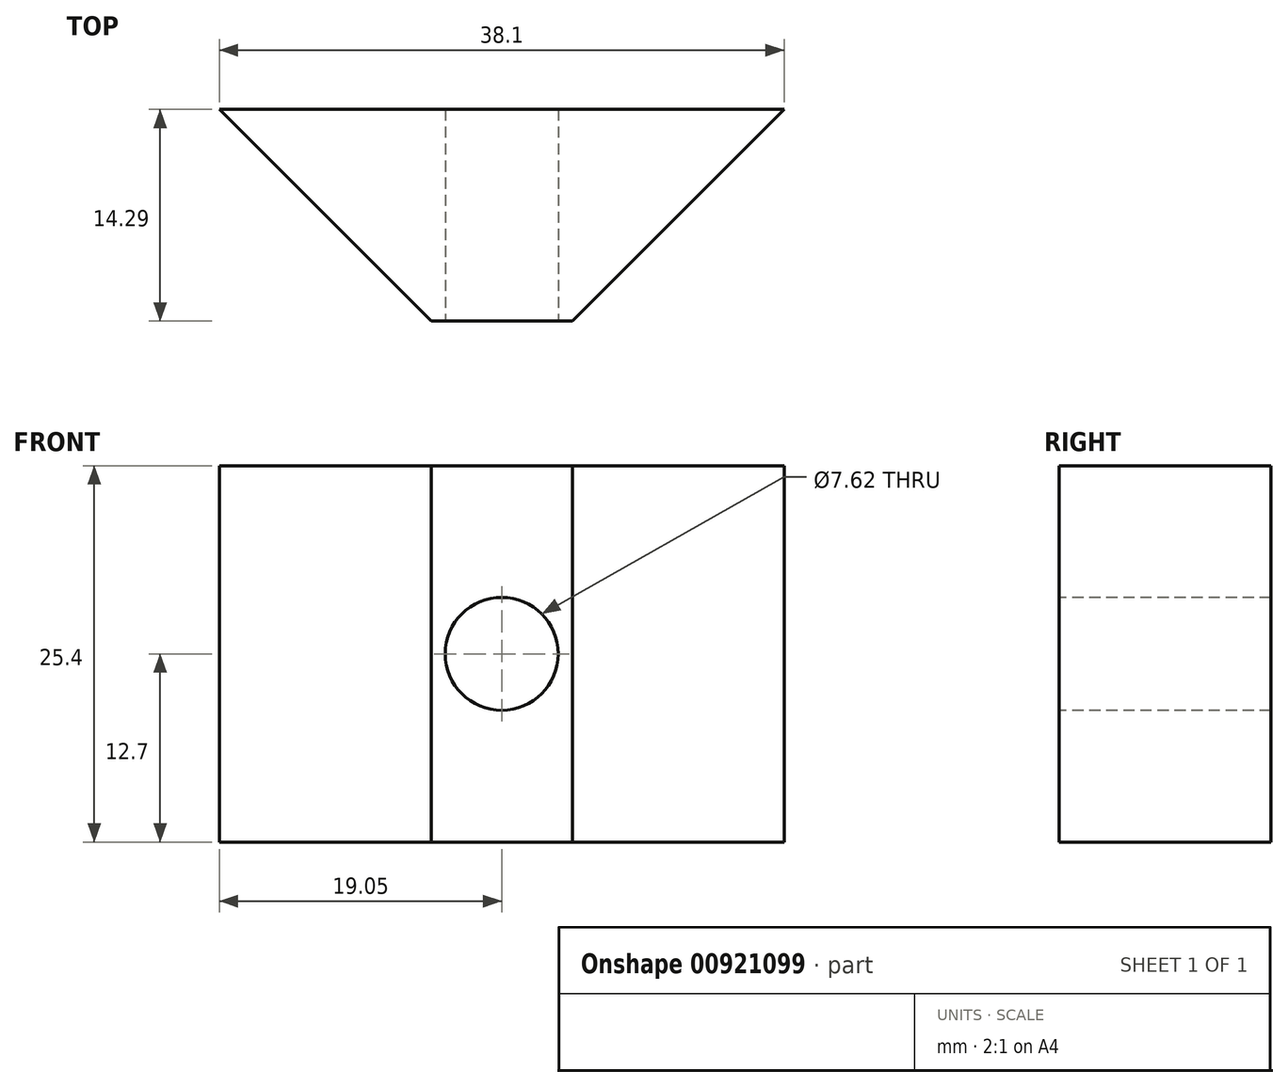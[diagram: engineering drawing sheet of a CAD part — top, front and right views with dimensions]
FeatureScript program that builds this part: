
annotation { "Feature Type Name" : "Feature", "Feature Type Description" : "" }
export const myFeature = defineFeature(function(context is Context, id is Id, definition is map)
    precondition{}
    {
        {
            var Q0;
            Q0=qCreatedBy(makeId("Top.planeOp"),FACE);
            var sketch = newSketch(context, id + "F0", { "sketchPlane" : qUnion([Q0])});
            skLineSegment(sketch, "E0", {"start": v(-4.76, 0) * mm, "end": v(4.76, 0) * mm});
            skLineSegment(sketch, "E1", {"start": v(4.76, 0) * mm, "end": v(19.05, 14.29) * mm});
            skLineSegment(sketch, "E2", {"start": v(-19.05, 14.29) * mm, "end": v(-4.76, 0) * mm});
            skLineSegment(sketch, "E3", {"start": v(-19.05, 14.29) * mm, "end": v(19.05, 14.29) * mm});
            skSolve(sketch);
        }
        {
            var Q0;
            Q0 = qSketchRegion(id + "F0", true);
            extrude(context, id + "F1", {"entities" : qUnion([Q0]), "endBound" : BoundingType.SYMMETRIC, "depth" : 25.4 * mm, "offsetDistance" : 25.4 * mm});
        }
        {
            var Q0;
            Q0=qCreatedBy(makeId("Front.planeOp"),FACE);
            var sketch = newSketch(context, id + "F2", { "sketchPlane" : qUnion([Q0])});
            skCircle(sketch, "E4", {"center": v(0, 0) * mm, "radius": 3.81 * mm});
            skSolve(sketch);
        }
        {
            var Q0;
            Q0 = qSketchRegion(id + "F2", true);
            extrude(context, id + "F3", {"entities" : qUnion([Q0]), "operationType" : NewBodyOperationType.REMOVE, "endBound" : BoundingType.THROUGH_ALL, "oppositeDirection" : true, "depth" : 25.4 * mm, "offsetDistance" : 25.4 * mm});
        }
    });
